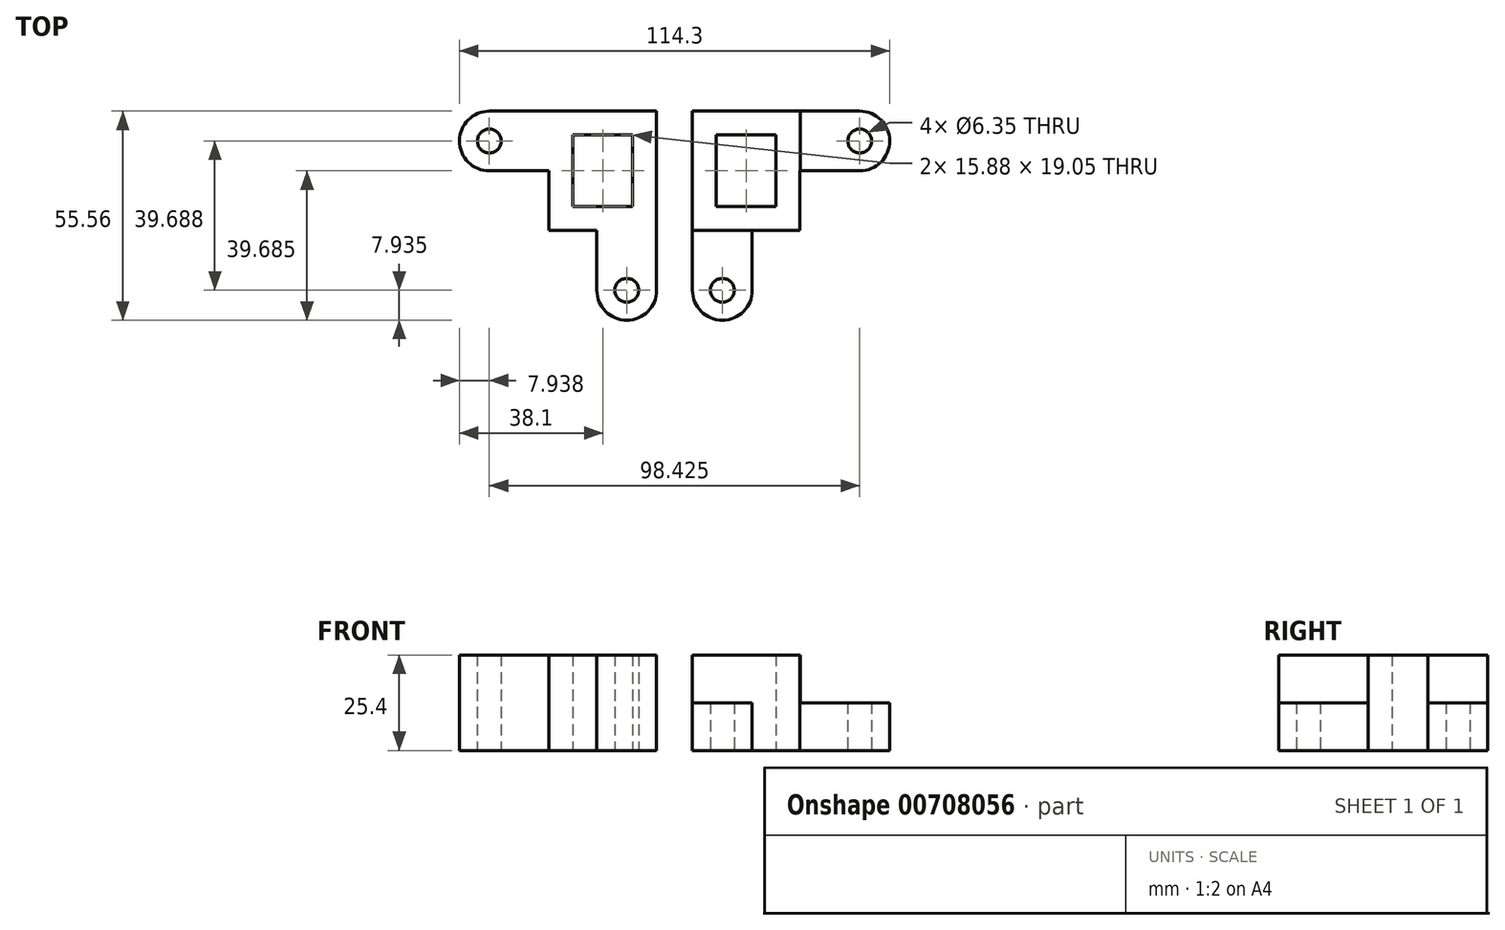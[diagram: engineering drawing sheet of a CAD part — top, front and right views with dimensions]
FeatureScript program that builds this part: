
annotation { "Feature Type Name" : "Feature", "Feature Type Description" : "" }
export const myFeature = defineFeature(function(context is Context, id is Id, definition is map)
    precondition{}
    {
        {
            var Q0;
            Q0=qCreatedBy(makeId("Top.planeOp"),FACE);
            var sketch = newSketch(context, id + "F0", { "sketchPlane" : qUnion([Q0])});
            skLineSegment(sketch, "E0.bottom", {"start": v(11.11, 0) * mm, "end": v(26.99, 0) * mm});
            skLineSegment(sketch, "E0.top", {"start": v(11.11, 19.05) * mm, "end": v(26.99, 19.05) * mm});
            skLineSegment(sketch, "E0.left", {"start": v(11.11, 0) * mm, "end": v(11.11, 19.05) * mm});
            skLineSegment(sketch, "E0.right", {"start": v(26.99, 0) * mm, "end": v(26.99, 19.05) * mm});
            skLineSegment(sketch, "E1.0", {"start": v(4.76, -6.35) * mm, "end": v(4.76, 25.4) * mm});
            skLineSegment(sketch, "E1.1", {"start": v(20.64, -6.35) * mm, "end": v(33.34, -6.35) * mm});
            skLineSegment(sketch, "E1.2", {"start": v(33.34, -6.35) * mm, "end": v(33.34, 9.53) * mm});
            skLineSegment(sketch, "E1.3", {"start": v(4.76, 25.4) * mm, "end": v(33.34, 25.4) * mm});
            skLineSegment(sketch, "E2.left", {"start": v(4.76, -6.35) * mm, "end": v(4.76, -22.22) * mm});
            skLineSegment(sketch, "E2.right", {"start": v(20.64, -6.35) * mm, "end": v(20.64, -22.22) * mm});
            skLineSegment(sketch, "E3.bottom", {"start": v(33.34, 25.4) * mm, "end": v(49.21, 25.4) * mm});
            skLineSegment(sketch, "E3.top", {"start": v(33.34, 9.53) * mm, "end": v(49.21, 9.53) * mm});
            skArc(sketch, "E4", {"start": v(4.76, -22.22) * mm, "mid": v(12.7, -30.16) * mm, "end": v(20.64, -22.22) * mm});
            skArc(sketch, "E5", {"start": v(49.21, 9.53) * mm, "mid": v(57.15, 17.46) * mm, "end": v(49.21, 25.4) * mm});
            skCircle(sketch, "E6", {"center": v(49.21, 17.46) * mm, "radius": 3.18 * mm});
            skCircle(sketch, "E7", {"center": v(12.7, -22.22) * mm, "radius": 3.18 * mm});
            skLineSegment(sketch, "E8.MirrorCS", {"start": v(-4.76, -6.35) * mm, "end": v(-4.76, 25.4) * mm});
            skLineSegment(sketch, "E9.MirrorCS", {"start": v(-4.76, 25.4) * mm, "end": v(-33.34, 25.4) * mm});
            skLineSegment(sketch, "E10.MirrorCS", {"start": v(-33.34, 25.4) * mm, "end": v(-49.21, 25.4) * mm});
            skArc(sketch, "E11.MirrorCS", {"start": v(-49.21, 9.53) * mm, "mid": v(-57.15, 17.46) * mm, "end": v(-49.21, 25.4) * mm});
            skLineSegment(sketch, "E12.MirrorCS", {"start": v(-33.34, 9.53) * mm, "end": v(-49.21, 9.53) * mm});
            skCircle(sketch, "E13.MirrorC", {"center": v(-49.21, 17.46) * mm, "radius": 3.18 * mm});
            skLineSegment(sketch, "E14.MirrorCS", {"start": v(-33.34, -6.35) * mm, "end": v(-33.34, 9.53) * mm});
            skLineSegment(sketch, "E15.MirrorCS", {"start": v(-20.64, -6.35) * mm, "end": v(-33.34, -6.35) * mm});
            skLineSegment(sketch, "E16.MirrorCS", {"start": v(-20.64, -6.35) * mm, "end": v(-20.64, -22.22) * mm});
            skArc(sketch, "E17.MirrorCS", {"start": v(-4.76, -22.22) * mm, "mid": v(-12.7, -30.16) * mm, "end": v(-20.64, -22.22) * mm});
            skLineSegment(sketch, "E18.MirrorCS", {"start": v(-4.76, -6.35) * mm, "end": v(-4.76, -22.22) * mm});
            skCircle(sketch, "E19.MirrorC", {"center": v(-12.7, -22.22) * mm, "radius": 3.18 * mm});
            skLineSegment(sketch, "E20.MirrorCS", {"start": v(-11.11, 0) * mm, "end": v(-26.99, 0) * mm});
            skLineSegment(sketch, "E21.MirrorCS", {"start": v(-11.11, 0) * mm, "end": v(-11.11, 19.05) * mm});
            skLineSegment(sketch, "E22.MirrorCS", {"start": v(-11.11, 19.05) * mm, "end": v(-26.99, 19.05) * mm});
            skLineSegment(sketch, "E23.MirrorCS", {"start": v(-26.99, 0) * mm, "end": v(-26.99, 19.05) * mm});
            skSolve(sketch);
        }
        {
            var Q0;
            Q0=makeQuery(id+"F0.imprint","IMPRINT",FACE,{"disambiguationData":[TD([[makeQuery(id+"F0.imprint","IMPRINT",EDGE,{"derivedFrom":sQuery(id+"F0.wireOp",EDGE,"E8.MirrorCS")}),1.0]])]});
            var Q1;
            Q1=makeQuery(id+"F0.imprint","IMPRINT",FACE,{"disambiguationData":[TD([[makeQuery(id+"F0.imprint","IMPRINT",EDGE,{"derivedFrom":sQuery(id+"F0.wireOp",EDGE,"E0.bottom")}),-1.0]])]});
            extrude(context, id + "F1", {"entities" : qUnion([Q0, Q1]), "depth" : 25.4 * mm, "offsetDistance" : 25.4 * mm});
        }
        {
            var Q0;
            Q0=makeQuery(id+"F1.opExtrude","CAP_FACE",FACE,{"disambiguationData":[OSD([sQuery(id+"F0.wireOp",EDGE,"E8.MirrorCS"),sQuery(id+"F0.wireOp",EDGE,"E9.MirrorCS"),sQuery(id+"F0.wireOp",EDGE,"E10.MirrorCS"),sQuery(id+"F0.wireOp",EDGE,"E11.MirrorCS"),sQuery(id+"F0.wireOp",EDGE,"E12.MirrorCS"),sQuery(id+"F0.wireOp",EDGE,"E13.MirrorC"),sQuery(id+"F0.wireOp",EDGE,"E14.MirrorCS"),sQuery(id+"F0.wireOp",EDGE,"E15.MirrorCS"),sQuery(id+"F0.wireOp",EDGE,"E16.MirrorCS"),sQuery(id+"F0.wireOp",EDGE,"E17.MirrorCS"),sQuery(id+"F0.wireOp",EDGE,"E18.MirrorCS"),sQuery(id+"F0.wireOp",EDGE,"E19.MirrorC"),sQuery(id+"F0.wireOp",EDGE,"E20.MirrorCS"),sQuery(id+"F0.wireOp",EDGE,"E21.MirrorCS"),sQuery(id+"F0.wireOp",EDGE,"E22.MirrorCS"),sQuery(id+"F0.wireOp",EDGE,"E23.MirrorCS")])],"isStart":false});
            var sketch = newSketch(context, id + "F2", { "sketchPlane" : qUnion([Q0])});
            skLineSegment(sketch, "E24.top", {"start": v(-20.64, -35.43) * mm, "end": v(0, -35.43) * mm});
            skLineSegment(sketch, "E24.left", {"start": v(-20.64, -6.35) * mm, "end": v(-20.64, -35.43) * mm});
            skLineSegment(sketch, "E25.bottom", {"start": v(-33.34, 9.53) * mm, "end": v(-62.7, 9.53) * mm});
            skLineSegment(sketch, "E25.top", {"start": v(-33.34, 29.69) * mm, "end": v(-62.7, 29.69) * mm});
            skLineSegment(sketch, "E25.left", {"start": v(-33.34, 9.53) * mm, "end": v(-33.34, 29.69) * mm});
            skLineSegment(sketch, "E25.right", {"start": v(-62.7, 9.53) * mm, "end": v(-62.7, 29.69) * mm});
            skLineSegment(sketch, "E26", {"start": v(-20.64, -6.35) * mm, "end": v(34.3, -6.35) * mm});
            skLineSegment(sketch, "E27", {"start": v(34.3, -6.35) * mm, "end": v(34.3, -35.7) * mm});
            skLineSegment(sketch, "E28", {"start": v(34.3, -35.7) * mm, "end": v(0, -35.43) * mm});
            skLineSegment(sketch, "E29.bottom", {"start": v(33.42, 8.88) * mm, "end": v(70.35, 8.88) * mm});
            skLineSegment(sketch, "E29.top", {"start": v(33.42, 36.75) * mm, "end": v(70.35, 36.75) * mm});
            skLineSegment(sketch, "E29.left", {"start": v(33.42, 8.88) * mm, "end": v(33.42, 36.75) * mm});
            skLineSegment(sketch, "E29.right", {"start": v(70.35, 8.88) * mm, "end": v(70.35, 36.75) * mm});
            skSolve(sketch);
        }
        {
            var Q0;
            {var subQ0=makeQuery(id+"F1.opExtrude","CAP_EDGE",EDGE,{"disambiguationData":[OSD([sQuery(id+"F0.wireOp",EDGE,"E11.MirrorCS")])],"isStart":false});Q0=makeQuery(id+"F2.imprint","IMPRINT",FACE,{"disambiguationData":[TD([[makeQuery(id+"F2.imprint","IMPRINT",EDGE,{"derivedFrom":subQ0}),-1.0]])]});}
            var Q1;
            {var subQ5=makeQuery(id+"F1.opExtrude","CAP_EDGE",EDGE,{"disambiguationData":[OSD([sQuery(id+"F0.wireOp",EDGE,"E17.MirrorCS")])],"isStart":false});Q1=makeQuery(id+"F2.imprint","IMPRINT",FACE,{"disambiguationData":[TD([[makeQuery(id+"F2.imprint","IMPRINT",EDGE,{"derivedFrom":subQ5}),-1.0]])]});}
            var Q2;
            {var subQ1=sQuery(id+"F2.wireOp",EDGE,"E24.top");Q2=makeQuery(id+"F2.imprint","IMPRINT",FACE,{"disambiguationData":[TD([[makeQuery(id+"F2.imprint","IMPRINT",EDGE,{"derivedFrom":subQ1}),1.0]])]});}
            var Q3;
            Q3=makeQuery(id+"F2.imprint","IMPRINT",FACE,{"disambiguationData":[TD([[makeQuery(id+"F2.imprint","IMPRINT",EDGE,{"derivedFrom":sQuery(id+"F2.wireOp",EDGE,"E29.bottom")}),1.0]])]});
            extrude(context, id + "F3", {"entities" : qUnion([Q0, Q1, Q2, Q3]), "operationType" : NewBodyOperationType.REMOVE, "oppositeDirection" : true, "depth" : 12.7 * mm, "offsetDistance" : 25.4 * mm});
        }
    });
